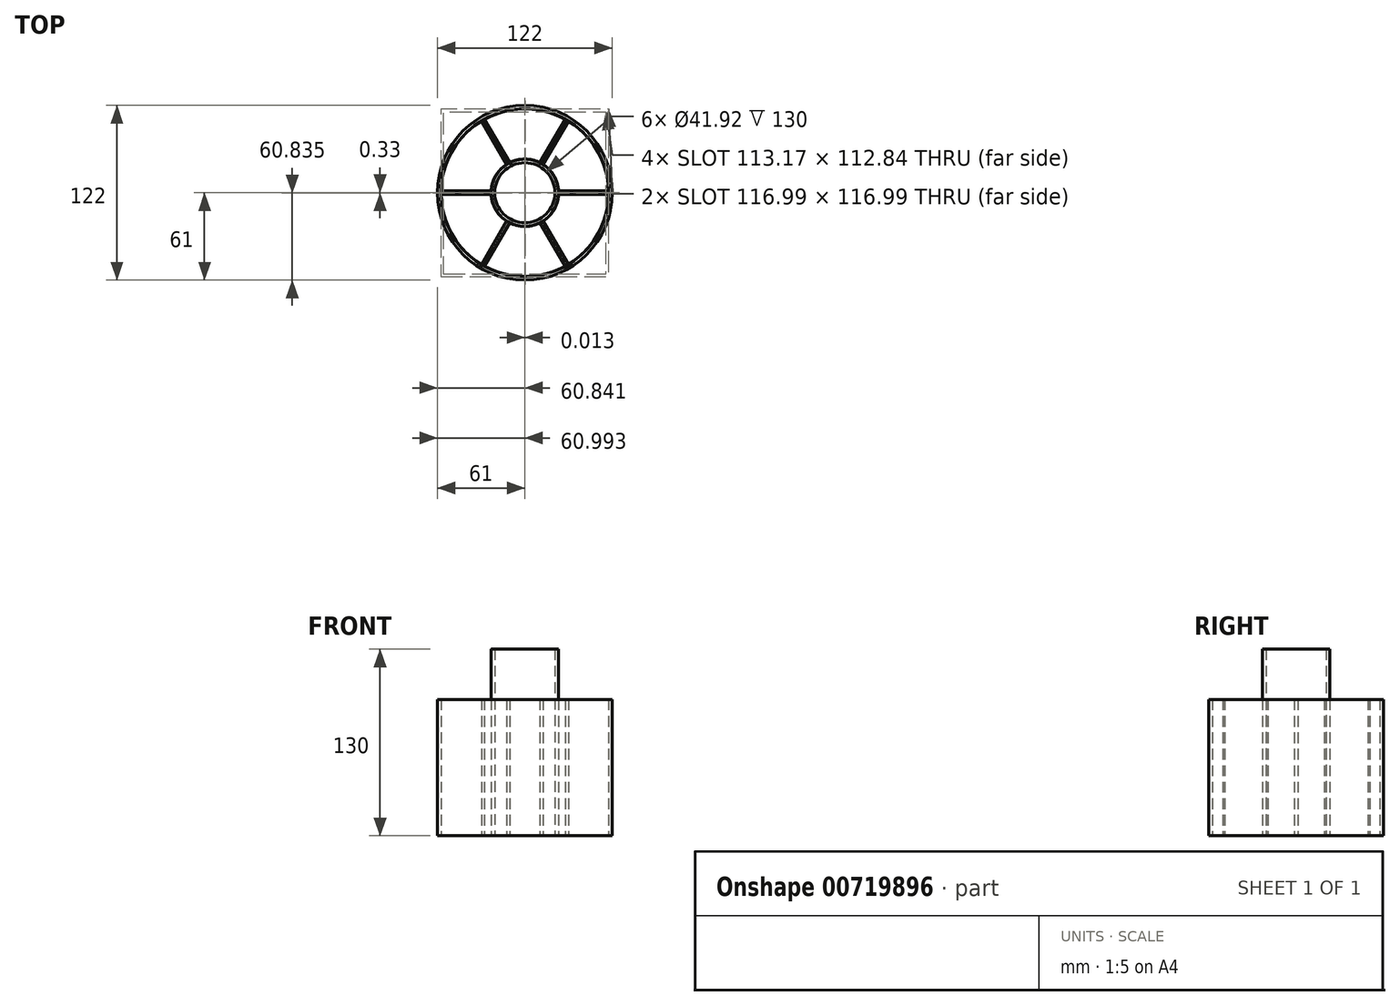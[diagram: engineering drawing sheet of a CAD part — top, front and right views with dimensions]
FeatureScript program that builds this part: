
annotation { "Feature Type Name" : "Feature", "Feature Type Description" : "" }
export const myFeature = defineFeature(function(context is Context, id is Id, definition is map)
    precondition{}
    {
        {
            var Q0;
            Q0=qCreatedBy(makeId("Top.planeOp"),FACE);
            var sketch = newSketch(context, id + "F0", { "sketchPlane" : qUnion([Q0])});
            skCircle(sketch, "E0", {"center": v(0, 0) * mm, "radius": 61 * mm});
            skCircle(sketch, "E1.0", {"center": v(0, 0) * mm, "radius": 58.5 * mm});
            skCircle(sketch, "E2", {"center": v(0, 0) * mm, "radius": 23.46 * mm});
            skLineSegment(sketch, "E3", {"start": v(-23.46, 0) * mm, "end": v(-61, 0) * mm});
            skLineSegment(sketch, "E4.0", {"start": v(-23.43, 1.25) * mm, "end": v(-60.99, 1.25) * mm});
            skLineSegment(sketch, "E5.0", {"start": v(-23.43, -1.25) * mm, "end": v(-60.99, -1.25) * mm});
            skCircle(sketch, "E6.0", {"center": v(0, 0) * mm, "radius": 20.96 * mm});
            skSolve(sketch);
        }
        {
            var Q0;
            {var subQ0=sQuery(id+"F0.wireOp",EDGE,"E4.0");var subQ1=sQuery(id+"F0.wireOp",EDGE,"E0");var subQ2=makeQuery(id+"F0.imprint","INTERSECT",VERTEX,{"derivedFrom":[subQ1,subQ0]});Q0=makeQuery(id+"F0.imprint","IMPRINT",FACE,{"disambiguationData":[TD([[makeQuery(id+"F0.imprint","IMPRINT",EDGE,{"disambiguationData":[TD([[subQ2,1.0]])],"derivedFrom":subQ1}),1.0]])]});}
            var Q1;
            {var subQ0=sQuery(id+"F0.wireOp",EDGE,"E3");var subQ1=sQuery(id+"F0.wireOp",EDGE,"E1.0");var subQ2=makeQuery(id+"F0.imprint","INTERSECT",VERTEX,{"derivedFrom":[subQ1,subQ0]});Q1=makeQuery(id+"F0.imprint","IMPRINT",FACE,{"disambiguationData":[TD([[makeQuery(id+"F0.imprint","IMPRINT",EDGE,{"disambiguationData":[TD([[subQ2,-1.0]])],"derivedFrom":subQ1}),1.0]])]});}
            var Q2;
            {var subQ0=sQuery(id+"F0.wireOp",EDGE,"E3");var subQ1=sQuery(id+"F0.wireOp",EDGE,"E1.0");var subQ2=makeQuery(id+"F0.imprint","INTERSECT",VERTEX,{"derivedFrom":[subQ1,subQ0]});Q2=makeQuery(id+"F0.imprint","IMPRINT",FACE,{"disambiguationData":[TD([[makeQuery(id+"F0.imprint","IMPRINT",EDGE,{"disambiguationData":[TD([[subQ2,1.0]])],"derivedFrom":subQ1}),1.0]])]});}
            var Q3;
            {var subQ0=sQuery(id+"F0.wireOp",EDGE,"E3");var subQ1=sQuery(id+"F0.wireOp",EDGE,"E0");var subQ2=makeQuery(id+"F0.imprint","INTERSECT",VERTEX,{"derivedFrom":[subQ1,subQ0]});Q3=makeQuery(id+"F0.imprint","IMPRINT",FACE,{"disambiguationData":[TD([[makeQuery(id+"F0.imprint","IMPRINT",EDGE,{"disambiguationData":[TD([[subQ2,-1.0]])],"derivedFrom":subQ1}),1.0]])]});}
            var Q4;
            {var subQ0=sQuery(id+"F0.wireOp",EDGE,"E3");var subQ1=sQuery(id+"F0.wireOp",EDGE,"E0");var subQ2=makeQuery(id+"F0.imprint","INTERSECT",VERTEX,{"derivedFrom":[subQ1,subQ0]});Q4=makeQuery(id+"F0.imprint","IMPRINT",FACE,{"disambiguationData":[TD([[makeQuery(id+"F0.imprint","IMPRINT",EDGE,{"disambiguationData":[TD([[subQ2,1.0]])],"derivedFrom":subQ1}),1.0]])]});}
            extrude(context, id + "F1", {"entities" : qUnion([Q0, Q1, Q2, Q3, Q4]), "depth" : 95 * mm, "offsetDistance" : 25 * mm});
        }
        {
            var Q0;
            Q0=makeQuery(id+"F0.imprint","IMPRINT",FACE,{"disambiguationData":[TD([[makeQuery(id+"F0.imprint","IMPRINT",EDGE,{"derivedFrom":sQuery(id+"F0.wireOp",EDGE,"E6.0")}),-1.0]])]});
            extrude(context, id + "F2", {"entities" : qUnion([Q0]), "operationType" : NewBodyOperationType.ADD, "depth" : 130 * mm, "offsetDistance" : 25 * mm});
        }
        {
            var Q0;
            Q0=makeQuery(id+"F1.opExtrude","SWEPT_BODY",BODY,{"disambiguationData":[OSD([sQuery(id+"F0.wireOp",EDGE,"E0"),sQuery(id+"F0.wireOp",EDGE,"E1.0"),sQuery(id+"F0.wireOp",EDGE,"E4.0"),sQuery(id+"F0.wireOp",EDGE,"E5.0")])]});
            var Q1;
            Q1=makeQuery(id+"F1.opExtrude","SWEPT_FACE",FACE,{"disambiguationData":[OSD([sQuery(id+"F0.wireOp",EDGE,"E1.0")])]});
            circularPattern(context, id + "F3", {"entities" : qUnion([Q0]), "axis" : qUnion([Q1]), "angle" : 360 * degree, "instanceCount" : 6, "equalSpace" : true});
        }
    });
